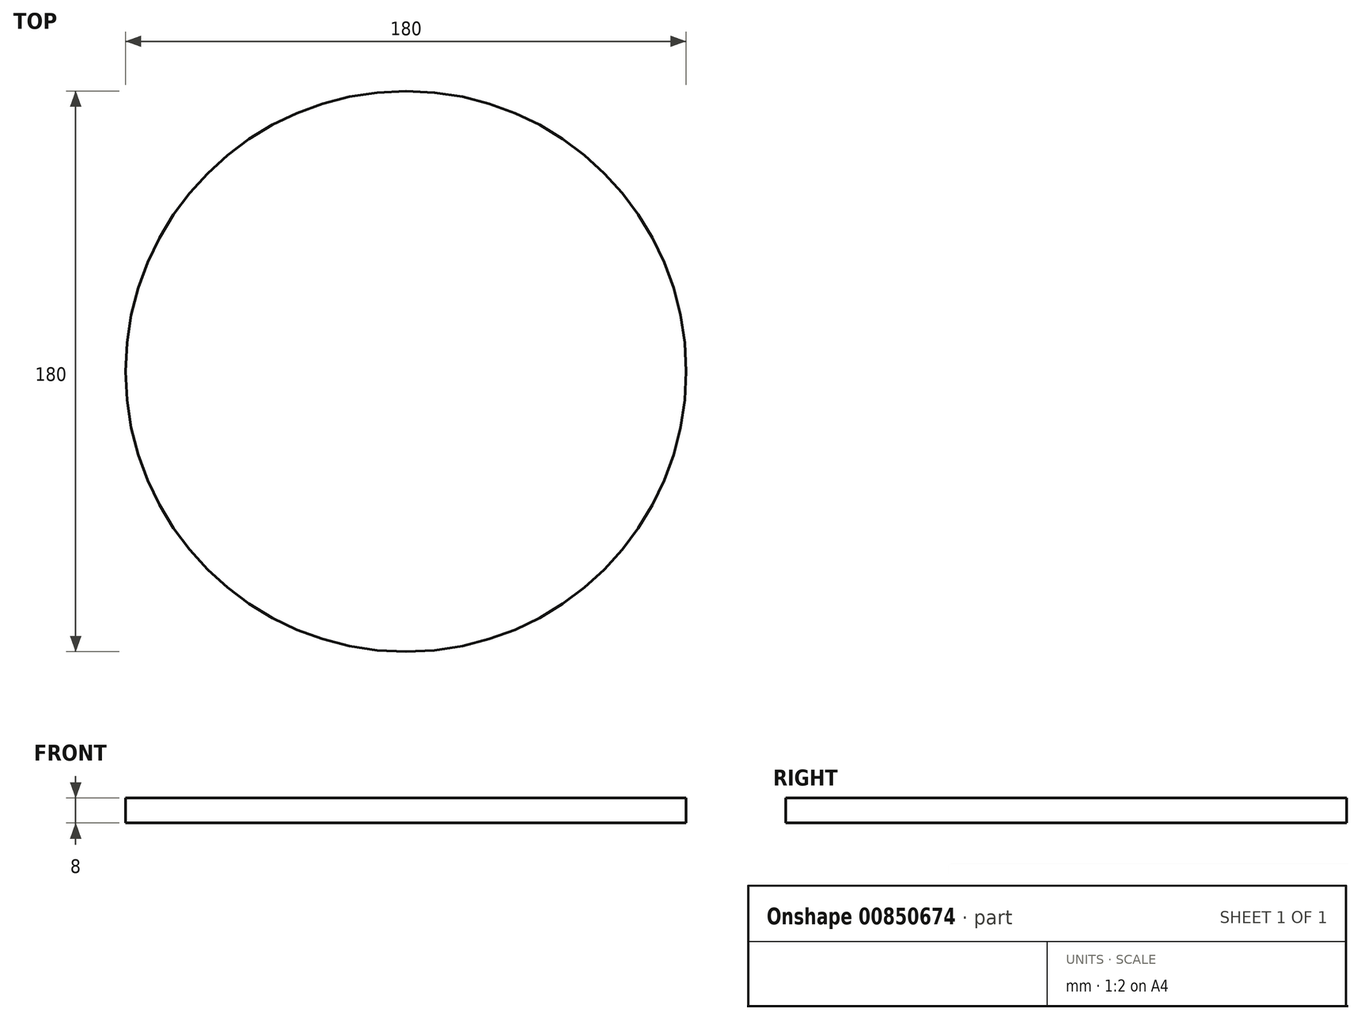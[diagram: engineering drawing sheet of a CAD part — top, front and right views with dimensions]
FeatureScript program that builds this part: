
annotation { "Feature Type Name" : "Feature", "Feature Type Description" : "" }
export const myFeature = defineFeature(function(context is Context, id is Id, definition is map)
    precondition{}
    {
        {
            var Q0;
            Q0=qCreatedBy(makeId("Top.planeOp"),FACE);
            var sketch = newSketch(context, id + "F0", { "sketchPlane" : qUnion([Q0])});
            skCircle(sketch, "E0", {"center": v(0, 0) * mm, "radius": 90 * mm});
            skSolve(sketch);
        }
        {
            var Q0;
            Q0=qSketchRegion(id+"F0",true);
            extrude(context, id + "F1", {"entities" : qUnion([Q0]), "depth" : 8 * mm, "offsetDistance" : 25 * mm});
        }
    });
